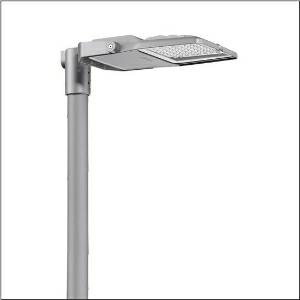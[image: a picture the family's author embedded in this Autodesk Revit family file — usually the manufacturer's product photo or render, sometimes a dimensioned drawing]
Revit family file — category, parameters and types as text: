
# Revit family: floodlight_fl_21_iq_mini___pl52_5xa7772d4d3a_25ab
name_source: partatom
category: Lighting Fixtures
units: mm (PartAtom-declared; Revit-internal decimal feet)

## family parameters
Cut with Voids When Loaded = No
Host = Face
Light Source = No
Part Type = Normal
Room Calculation Point = No
Round Connector Dimension = Use Diameter
Shared = No

## types (1)
- --- (1 x LED, 18610 lm, 143 W, 4000K)
    Apparent Load = 143 VA
    CIE Flux Codes = 26 60 98 100 100
    Color Rendering = 70
    Color Temperature = 4000K
    Default Elevation = 1800 mm
    Description = Floodlight FL 21 iQ mini, floodlight, primary light control with lens, of PMMA, primary optical cover: protective disc, of toughened safety glass, transparent, light distribution: PL52, light emission: direct distribution, installation type: surface-mounted, LED, High Power LED, rated luminous flux: 18.610lm, luminous efficacy: 130lm/W, light colour: 740, colour temperature: 4000K, control gear: iQ Street-Remote/DALI, control: Auto-Match, Temp-Guard, Night-Set, Smart-Wire, Desk-Remote (wireless, voltage-free reading and setting of iQ features in the workshop via application-optimized NFC function/RFID function), optimised constant luminous flux control (CLO 2.0), Light-Fading, Lumen-Switch, with terminal, 6-pole, mains connection: 220..240V, AC, 50/60Hz, start of lifetime: 143W, end of service life: 152W, reduction: 61W, luminaire housing, of diecast aluminium, powder-coated, Siteco® metallic grey (DB 702S), corrosivity category C5 mid according to DIN EN ISO 12944, suitable for swimming pools, chlorine-resistant, sealing non-destructively replaceable, please order mast flange separately, mast bracket, of steel, galvanised, powder-coated, protection rating (complete): IP66, insulation class (complete): insulation class II (safety insulation), certification: CE, ENEC, VDE, protection symbol: D, impact resistance: IK08, permissible operating ambient temperature: -40..+40°C, permissible operating ambient temperature for outdoor applications: -40..+50°C, standard: DIN EN 12944, LABS conformity tested according to VDMA 24364:2018-05, packaging unit: 1 piece

Light Distribution: PL52
    Height = 70 mm
    Lamp = 1 x LED
    Lamp Light Flux = 18610 lm
    Lamp Power = 143 W
    Lamp count = 1
    Length = 485 mm
    Luminous efficacy = 130 lm/W
    Manufacturer = Siteco
    ModVariant = No
    Model = 5XA7772D4D3A
    Number of Poles = 1
    OnlyDefault = Yes
    Power Factor = 1
    Product Name = Floodlight FL 21 iQ mini | PL52
    Product group = floodlight | pylon annexe
    ProductGroupID = 6201
    Protection Class = Protection class II
    Protection Degree = IP 66
    RLX_Detail_Level = 1
    RLX_Emergency_Light_Flux = 0 lm
    RLX_Emergency_Type = 0
    RLX_Emergency_Type_DB = No
    RlxData = <blob elided: 101925 chars, md5=9b547153>
    Socket = socket
    Standby Power = 0 W
    System Light Flux = 18610 lm
    System Power = 143 W
    Type Comments = factory setting: luminous flux: 100 % | dim-lin: 254 | 730 mA
    Type Image = l_1007125.jpg
    URL = http://relux.com
    VarID = @adj_185017
    Voltage = 0 V
    Weight = 0.00 kg
    Width = 337 mm

## geometry (parser evidence)
native form markers: Blend x4, Sweep x11
no freeform markers — native parametric forms only
